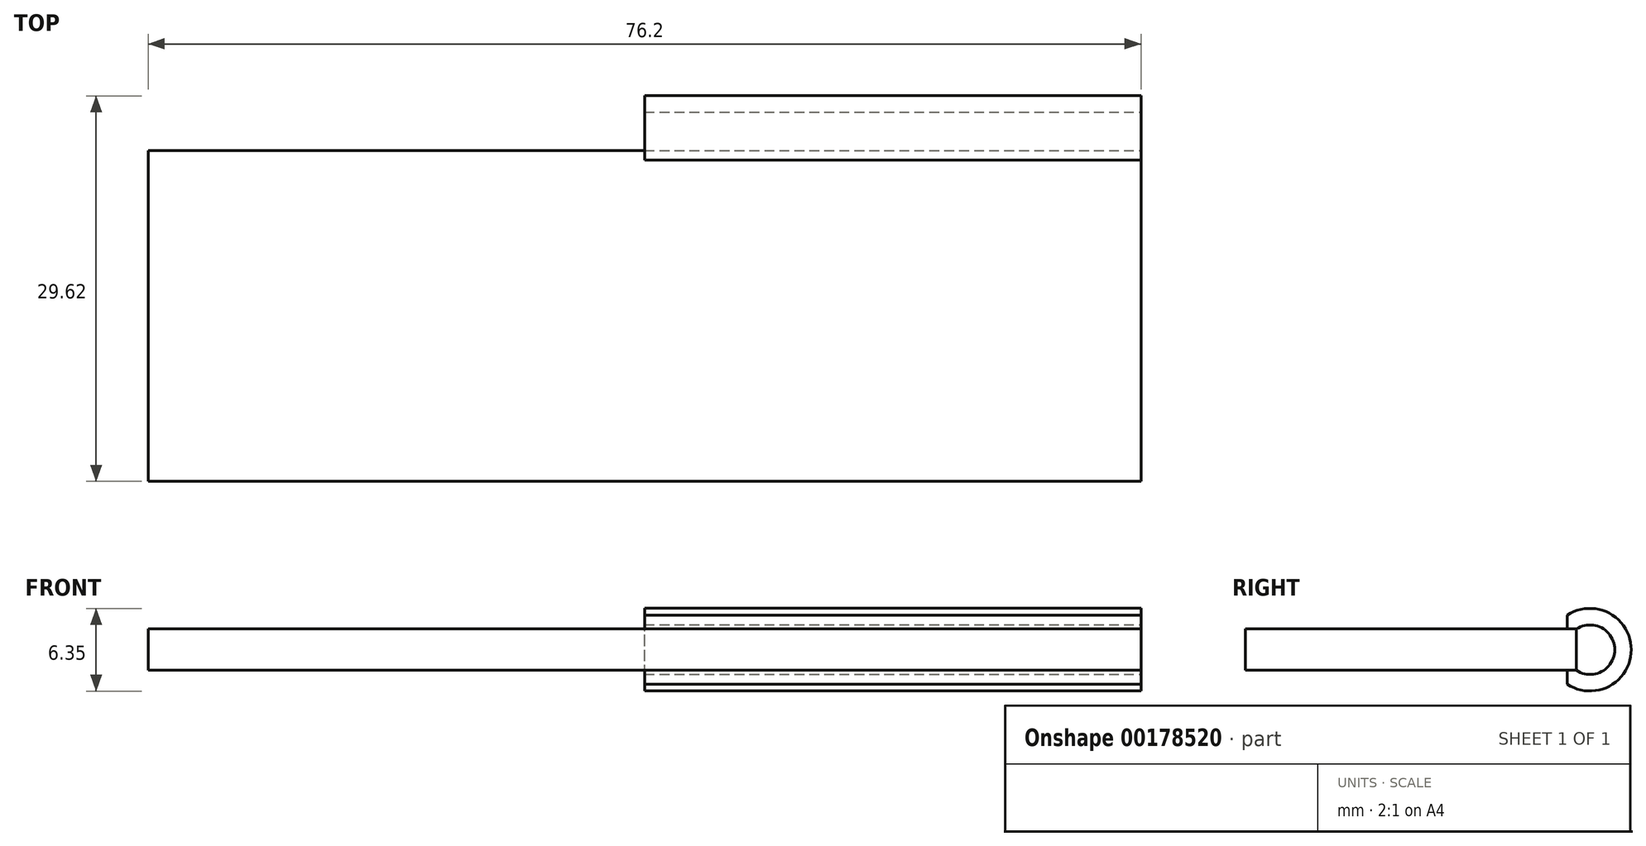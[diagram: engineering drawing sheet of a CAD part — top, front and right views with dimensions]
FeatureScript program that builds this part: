
annotation { "Feature Type Name" : "Feature", "Feature Type Description" : "" }
export const myFeature = defineFeature(function(context is Context, id is Id, definition is map)
    precondition{}
    {
        {
            var Q0;
            Q0=qCreatedBy(makeId("Top.planeOp"),FACE);
            var sketch = newSketch(context, id + "F0", { "sketchPlane" : qUnion([Q0])});
            skLineSegment(sketch, "E0.bottom", {"start": v(38.1, -12.7) * mm, "end": v(-38.1, -12.7) * mm});
            skLineSegment(sketch, "E0.top", {"start": v(38.1, 12.7) * mm, "end": v(-38.1, 12.7) * mm});
            skLineSegment(sketch, "E0.left", {"start": v(38.1, -12.7) * mm, "end": v(38.1, 12.7) * mm});
            skLineSegment(sketch, "E0.right", {"start": v(-38.1, -12.7) * mm, "end": v(-38.1, 12.7) * mm});
            skPoint(sketch, "E0.middle", {"position": v(0, 0) * mm});
            skSolve(sketch);
        }
        {
            var Q0;
            Q0=makeQuery(id+"F0.imprint","IMPRINT",FACE,{"disambiguationData":[TD([[makeQuery(id+"F0.imprint","IMPRINT",EDGE,{"derivedFrom":sQuery(id+"F0.wireOp",EDGE,"E0.bottom")}),-1.0]])]});
            extrude(context, id + "F1", {"entities" : qUnion([Q0]), "depth" : 3.17 * mm});
        }
        {
            var Q0;
            Q0=makeQuery(id+"F1.opExtrude","SWEPT_FACE",FACE,{"disambiguationData":[OSD([sQuery(id+"F0.wireOp",EDGE,"E0.left")])]});
            var sketch = newSketch(context, id + "F2", { "sketchPlane" : qUnion([Q0])});
            skArc(sketch, "E1", {"start": v(12.7, 0) * mm, "mid": v(15.65, 1.59) * mm, "end": v(12.7, 3.18) * mm});
            skArc(sketch, "E2.0", {"start": v(12, -1.06) * mm, "mid": v(16.92, 1.59) * mm, "end": v(12, 4.23) * mm});
            skLineSegment(sketch, "E3", {"start": v(12, 4.23) * mm, "end": v(12.7, 3.18) * mm});
            skLineSegment(sketch, "E4", {"start": v(12, -1.06) * mm, "end": v(12.7, 0) * mm});
            skLineSegment(sketch, "E5", {"start": v(12, 4.23) * mm, "end": v(12, 3.18) * mm});
            skLineSegment(sketch, "E6", {"start": v(12, -1.06) * mm, "end": v(12, 0) * mm});
            skSolve(sketch);
        }
        {
            var Q0;
            Q0=makeQuery(id+"F2.imprint","IMPRINT",FACE,{"disambiguationData":[TD([[makeQuery(id+"F2.imprint","IMPRINT",EDGE,{"derivedFrom":sQuery(id+"F2.wireOp",EDGE,"E1")}),-1.0]])]});
            var Q1;
            {var subQ0=sQuery(id+"F2.wireOp",EDGE,"E3");Q1=makeQuery(id+"F2.imprint","IMPRINT",FACE,{"disambiguationData":[TD([[makeQuery(id+"F2.imprint","IMPRINT",EDGE,{"derivedFrom":subQ0}),-1.0]])]});}
            var Q2;
            {var subQ0=sQuery(id+"F2.wireOp",EDGE,"E4");Q2=makeQuery(id+"F2.imprint","IMPRINT",FACE,{"disambiguationData":[TD([[makeQuery(id+"F2.imprint","IMPRINT",EDGE,{"derivedFrom":subQ0}),1.0]])]});}
            extrude(context, id + "F3", {"entities" : qUnion([Q0, Q1, Q2]), "oppositeDirection" : true, "depth" : 38.1 * mm});
        }
    });
